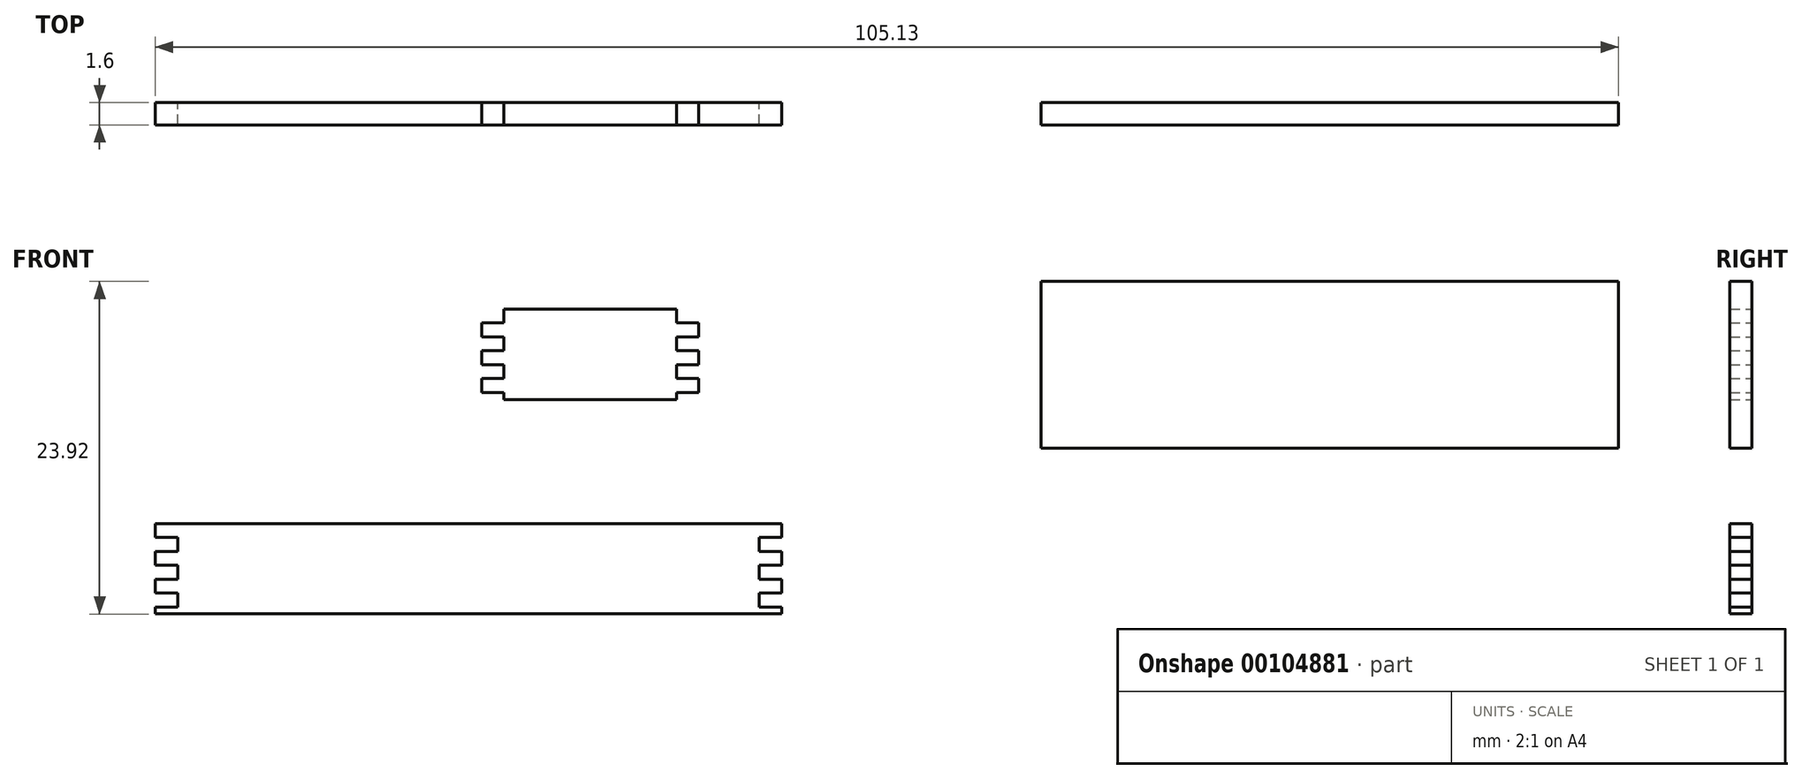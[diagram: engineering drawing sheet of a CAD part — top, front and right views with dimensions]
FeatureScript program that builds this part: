
annotation { "Feature Type Name" : "Feature", "Feature Type Description" : "" }
export const myFeature = defineFeature(function(context is Context, id is Id, definition is map)
    precondition{}
    {
        {
            var Q0;
            Q0=qCreatedBy(makeId("Front.planeOp"),FACE);
            var sketch = newSketch(context, id + "F0", { "sketchPlane" : qUnion([Q0])});
            skLineSegment(sketch, "E0.bottom", {"start": v(-26.81, 42.46) * mm, "end": v(-14.41, 42.46) * mm});
            skLineSegment(sketch, "E0.top", {"start": v(-26.81, 35.96) * mm, "end": v(-14.41, 35.96) * mm});
            skLineSegment(sketch, "E0.left", {"start": v(-28.41, 41.46) * mm, "end": v(-28.41, 40.46) * mm});
            skLineSegment(sketch, "E0.right", {"start": v(-12.81, 41.46) * mm, "end": v(-12.81, 40.46) * mm});
            skLineSegment(sketch, "E1.bottom", {"start": v(11.78, 44.45) * mm, "end": v(53.28, 44.45) * mm});
            skLineSegment(sketch, "E1.top", {"start": v(11.78, 32.45) * mm, "end": v(53.28, 32.45) * mm});
            skLineSegment(sketch, "E1.left", {"start": v(11.78, 44.45) * mm, "end": v(11.78, 32.45) * mm});
            skLineSegment(sketch, "E1.right", {"start": v(53.28, 44.45) * mm, "end": v(53.28, 32.45) * mm});
            skLineSegment(sketch, "E2", {"start": v(-26.81, 42.46) * mm, "end": v(-26.81, 41.46) * mm});
            skLineSegment(sketch, "E3", {"start": v(-14.41, 42.46) * mm, "end": v(-14.41, 41.46) * mm});
            skLineSegment(sketch, "E4", {"start": v(-28.41, 36.46) * mm, "end": v(-26.81, 36.46) * mm});
            skLineSegment(sketch, "E5", {"start": v(-28.41, 37.46) * mm, "end": v(-26.81, 37.46) * mm});
            skLineSegment(sketch, "E6", {"start": v(-28.41, 38.46) * mm, "end": v(-26.81, 38.46) * mm});
            skLineSegment(sketch, "E7", {"start": v(-28.41, 39.46) * mm, "end": v(-26.81, 39.46) * mm});
            skLineSegment(sketch, "E8", {"start": v(-28.41, 40.46) * mm, "end": v(-26.81, 40.46) * mm});
            skLineSegment(sketch, "E9", {"start": v(-28.41, 41.46) * mm, "end": v(-26.81, 41.46) * mm});
            skLineSegment(sketch, "E10.trimOffspring", {"start": v(-14.41, 41.46) * mm, "end": v(-12.81, 41.46) * mm});
            skLineSegment(sketch, "E11.trimOffspring", {"start": v(-14.41, 40.46) * mm, "end": v(-12.81, 40.46) * mm});
            skLineSegment(sketch, "E12.trimOffspring", {"start": v(-14.41, 39.46) * mm, "end": v(-12.81, 39.46) * mm});
            skLineSegment(sketch, "E13.trimOffspring", {"start": v(-14.41, 38.46) * mm, "end": v(-12.81, 38.46) * mm});
            skLineSegment(sketch, "E14.trimOffspring", {"start": v(-14.41, 37.46) * mm, "end": v(-12.81, 37.46) * mm});
            skLineSegment(sketch, "E15.trimOffspring", {"start": v(-14.41, 36.46) * mm, "end": v(-12.81, 36.46) * mm});
            skLineSegment(sketch, "E16.trimOffspring", {"start": v(-12.81, 37.46) * mm, "end": v(-12.81, 36.46) * mm});
            skLineSegment(sketch, "E17.trimOffspring", {"start": v(-12.81, 39.46) * mm, "end": v(-12.81, 38.46) * mm});
            skLineSegment(sketch, "E18.trimOffspring", {"start": v(-28.41, 39.46) * mm, "end": v(-28.41, 38.46) * mm});
            skLineSegment(sketch, "E19.trimOffspring", {"start": v(-28.41, 37.46) * mm, "end": v(-28.41, 36.46) * mm});
            skLineSegment(sketch, "E20.trimOffspring", {"start": v(-14.41, 40.46) * mm, "end": v(-14.41, 39.46) * mm});
            skLineSegment(sketch, "E21.trimOffspring", {"start": v(-26.81, 40.46) * mm, "end": v(-26.81, 39.46) * mm});
            skLineSegment(sketch, "E22.trimOffspring", {"start": v(-26.81, 38.46) * mm, "end": v(-26.81, 37.46) * mm});
            skLineSegment(sketch, "E23.trimOffspring", {"start": v(-26.81, 36.46) * mm, "end": v(-26.81, 35.96) * mm});
            skLineSegment(sketch, "E24.trimOffspring", {"start": v(-14.41, 36.46) * mm, "end": v(-14.41, 35.96) * mm});
            skLineSegment(sketch, "E25.trimOffspring", {"start": v(-14.41, 38.46) * mm, "end": v(-14.41, 37.46) * mm});
            skLineSegment(sketch, "E26.bottom", {"start": v(-51.85, 27.03) * mm, "end": v(-6.85, 27.03) * mm});
            skLineSegment(sketch, "E26.top", {"start": v(-51.85, 20.53) * mm, "end": v(-6.85, 20.53) * mm});
            skLineSegment(sketch, "E26.left", {"start": v(-51.85, 27.03) * mm, "end": v(-51.85, 26.03) * mm});
            skLineSegment(sketch, "E26.right", {"start": v(-6.85, 27.03) * mm, "end": v(-6.85, 26.03) * mm});
            skLineSegment(sketch, "E27", {"start": v(-50.25, 26.03) * mm, "end": v(-50.25, 25.03) * mm});
            skLineSegment(sketch, "E28", {"start": v(-8.45, 26.03) * mm, "end": v(-8.45, 25.03) * mm});
            skLineSegment(sketch, "E29", {"start": v(-51.85, 21.03) * mm, "end": v(-50.25, 21.03) * mm});
            skLineSegment(sketch, "E30", {"start": v(-51.85, 22.03) * mm, "end": v(-50.25, 22.03) * mm});
            skLineSegment(sketch, "E31", {"start": v(-51.85, 25.03) * mm, "end": v(-50.25, 25.03) * mm});
            skLineSegment(sketch, "E32", {"start": v(-6.85, 24.03) * mm, "end": v(-8.45, 24.03) * mm});
            skLineSegment(sketch, "E33", {"start": v(-51.85, 23.03) * mm, "end": v(-50.25, 23.03) * mm});
            skLineSegment(sketch, "E34", {"start": v(-51.85, 26.03) * mm, "end": v(-50.25, 26.03) * mm});
            skLineSegment(sketch, "E35.trimOffspring", {"start": v(-8.45, 26.03) * mm, "end": v(-6.85, 26.03) * mm});
            skLineSegment(sketch, "E36.trimOffspring", {"start": v(-8.45, 25.03) * mm, "end": v(-6.85, 25.03) * mm});
            skLineSegment(sketch, "E37.trimOffspring", {"start": v(-50.25, 24.03) * mm, "end": v(-51.85, 24.03) * mm});
            skLineSegment(sketch, "E38.trimOffspring", {"start": v(-8.45, 23.03) * mm, "end": v(-6.85, 23.03) * mm});
            skLineSegment(sketch, "E39.trimOffspring", {"start": v(-8.45, 22.03) * mm, "end": v(-6.85, 22.03) * mm});
            skLineSegment(sketch, "E40.trimOffspring", {"start": v(-8.45, 21.03) * mm, "end": v(-6.85, 21.03) * mm});
            skLineSegment(sketch, "E41.trimOffspring", {"start": v(-51.85, 21.03) * mm, "end": v(-51.85, 20.53) * mm});
            skLineSegment(sketch, "E42.trimOffspring", {"start": v(-51.85, 23.03) * mm, "end": v(-51.85, 22.03) * mm});
            skLineSegment(sketch, "E43.trimOffspring", {"start": v(-51.85, 25.03) * mm, "end": v(-51.85, 24.03) * mm});
            skLineSegment(sketch, "E44.trimOffspring", {"start": v(-50.25, 22.03) * mm, "end": v(-50.25, 21.03) * mm});
            skLineSegment(sketch, "E45.trimOffspring", {"start": v(-50.25, 24.03) * mm, "end": v(-50.25, 23.03) * mm});
            skLineSegment(sketch, "E46.trimOffspring", {"start": v(-6.85, 21.03) * mm, "end": v(-6.85, 20.53) * mm});
            skLineSegment(sketch, "E47.trimOffspring", {"start": v(-8.45, 22.03) * mm, "end": v(-8.45, 21.03) * mm});
            skLineSegment(sketch, "E48.trimOffspring", {"start": v(-6.85, 23.03) * mm, "end": v(-6.85, 22.03) * mm});
            skLineSegment(sketch, "E49.trimOffspring", {"start": v(-8.45, 24.03) * mm, "end": v(-8.45, 23.03) * mm});
            skLineSegment(sketch, "E50.trimOffspring", {"start": v(-6.85, 25.03) * mm, "end": v(-6.85, 24.03) * mm});
            skSolve(sketch);
        }
        {
            var Q0;
            Q0=makeQuery(id+"F0.imprint","IMPRINT",FACE,{"disambiguationData":[TD([[makeQuery(id+"F0.imprint","IMPRINT",EDGE,{"derivedFrom":sQuery(id+"F0.wireOp",EDGE,"E0.bottom")}),-1.0]])]});
            var Q1;
            Q1=makeQuery(id+"F0.imprint","IMPRINT",FACE,{"disambiguationData":[TD([[makeQuery(id+"F0.imprint","IMPRINT",EDGE,{"derivedFrom":sQuery(id+"F0.wireOp",EDGE,"E1.bottom")}),-1.0]])]});
            var Q2;
            Q2=makeQuery(id+"F0.imprint","IMPRINT",FACE,{"disambiguationData":[TD([[makeQuery(id+"F0.imprint","IMPRINT",EDGE,{"derivedFrom":sQuery(id+"F0.wireOp",EDGE,"E26.bottom")}),-1.0]])]});
            extrude(context, id + "F1", {"entities" : qUnion([Q0, Q1, Q2]), "depth" : 1.6 * mm});
        }
    });
